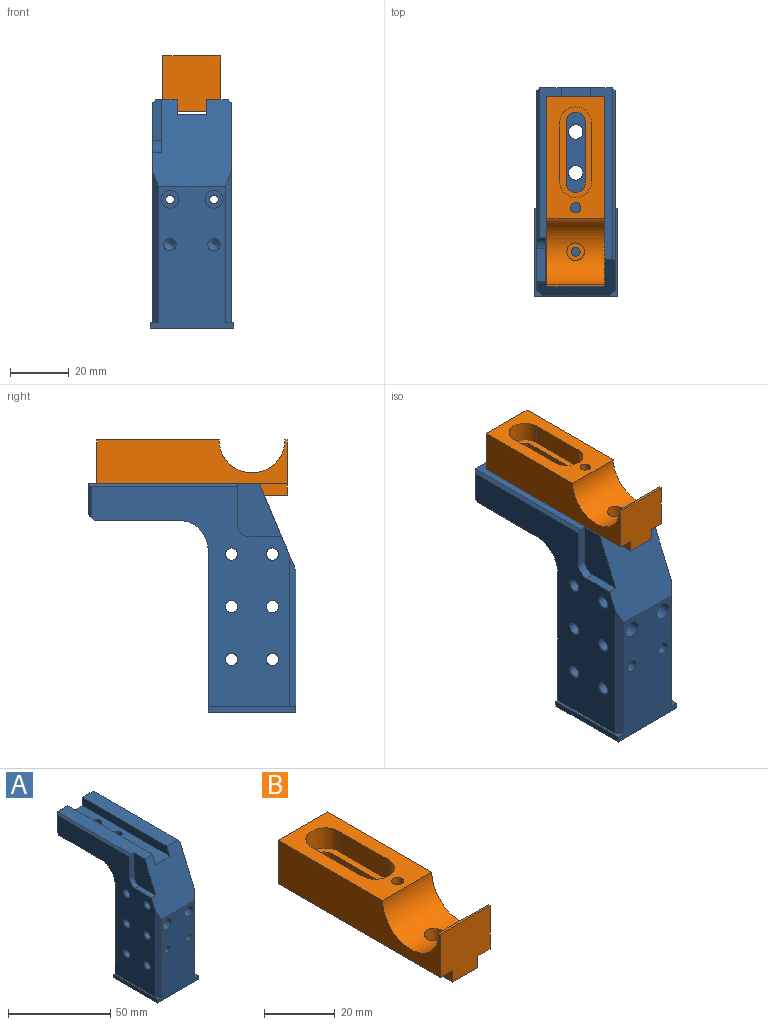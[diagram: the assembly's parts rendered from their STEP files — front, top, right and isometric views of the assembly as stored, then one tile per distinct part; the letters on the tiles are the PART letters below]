
ASSEMBLY  parts=2 mates=3
PART A: 53 faces, bbox 28.5x71x78 mm
  f0: cylinder r=10mm len=26.8mm, axis (-1,0,0), area 420mm2, adj f6,f7,f12,f14,f29
  f1: plane 58.48x7.3mm, normal (0,0,1), area 411.9mm2, adj f2,f3,f15,f17,f20,f48
  f2: plane 24.8x10.5mm, normal (0,1,0), area 210.4mm2, adj f1,f4,f19,f20,f21,f46,f51,f52
  f3: plane 29.5x26.8mm, normal (0,-0.92,0.39), area 735.1mm2, adj f1,f4,f8,f12,f14,f16,f17,f19
  f4: plane 58.48x7.5mm, normal (0,0,1), area 438.6mm2, adj f2,f3,f19,f47
  f5: plane 30x2mm, normal (-1,0,0), area 60mm2, adj f7,f8,f9,f13
  f6: plane 29x26.8mm, normal (0,0,-1), area 739mm2, adj f0,f12,f14,f28,f29,f46
  f7: plane 55.5x28.5mm, normal (0,1,0), area 1476.7mm2, adj f0,f5,f9,f10,f11,f12,f13,f14
  f8: plane 48.5x28.5mm, normal (0,-1,0), area 1032.9mm2, adj f3,f5,f9,f10,f11,f13,f30,f32
  f9: plane 30x28.5mm, normal (0,0,-1), area 799mm2, adj f5,f7,f8,f10,f41,f43,f44
  f10: plane 30x2mm, normal (1,0,0), area 60mm2, adj f7,f8,f9,f11
  f11: plane 30x2.85mm, normal (0,0,1), area 27.5mm2, adj f7,f8,f10,f12,f49
  f12: plane 75x68mm, normal (1,0,0), area 2377.7mm2, adj f0,f3,f6,f7,f11,f22,f23,f24
  f13: plane 30x2.85mm, normal (0,0,1), area 27.5mm2, adj f5,f7,f8,f14,f50
  f14: plane 75x68mm, normal (-1,0,0), area 2185.5mm2, adj f0,f3,f6,f7,f13,f15,f16,f18
  f15: plane 14x3mm, normal (0,-1,0), area 41.5mm2, adj f1,f14,f17,f18,f48
  f16: plane 11.12x3mm, normal (0,0,1), area 33.4mm2, adj f3,f14,f17,f18
  f17: plane 18x15.12mm, normal (-1,0,0), area 199.9mm2, adj f1,f3,f15,f16,f18
  f18: cylinder r=4mm len=4mm, axis (1,0,0), area 18.8mm2, adj f14,f15,f16,f17
  f19: plane 60.6x5mm, normal (-1,0,0), area 297.7mm2, adj f2,f3,f4,f21
  f20: plane 60.6x5mm, normal (1,0,0), area 297.7mm2, adj f1,f2,f3,f21
  f21: plane 60.6x10mm, normal (0,0,1), area 566.7mm2, adj f2,f3,f19,f20,f28,f29
  f22: cylinder r=2.1mm len=26.8mm, axis (1,0,0), area 353.6mm2, adj f12,f14
  f23: cylinder r=2.1mm len=26.8mm, axis (1,0,0), area 353.6mm2, adj f12,f14
  f24: cylinder r=2.1mm len=26.8mm, axis (1,0,0), area 353.6mm2, adj f12,f14
  f25: cylinder r=2.1mm len=26.8mm, axis (1,0,0), area 353.6mm2, adj f12,f14
  f26: cylinder r=2.1mm len=26.8mm, axis (1,0,0), area 353.6mm2, adj f12,f14
  f27: cylinder r=2.1mm len=26.8mm, axis (1,0,0), area 353.6mm2, adj f12,f14
  f28: cylinder r=2.5mm len=7.5mm, axis (0,0,1), area 117.8mm2, adj f6,f21
  f29: cylinder r=2.5mm len=7.5mm, axis (0,0,1), area 117.8mm2, adj f0,f6,f21
  f30: cylinder r=3mm len=6mm, axis (0,-1,0), area 84.8mm2, adj f8,f31
  f31: plane 6x6mm, normal (0,-1,0), area 21.2mm2, adj f30,f35
  f32: cylinder r=3mm len=6mm, axis (0,-1,0), area 84.8mm2, adj f8,f33
  f33: plane 6x6mm, normal (0,-1,0), area 21.2mm2, adj f32,f34
  f34: cylinder r=1.5mm len=25.5mm, axis (0,-1,0), area 240.3mm2, adj f7,f33
  f35: cylinder r=1.5mm len=25.5mm, axis (0,-1,0), area 240.3mm2, adj f7,f31
  f36: cone r=0mm half-angle=59deg, axis (0,-1,0), area 16.2mm2, adj f37
  f37: cylinder r=2.1mm len=15mm, axis (0,-1,0), area 197.9mm2, adj f8,f36
  f38: cone r=0mm half-angle=59deg, axis (0,-1,0), area 16.2mm2, adj f39
  f39: cylinder r=2.1mm len=15mm, axis (0,-1,0), area 197.9mm2, adj f8,f38
  f40: cone r=0mm half-angle=59deg, axis (0,0,-1), area 16.2mm2, adj f41
  f41: cylinder r=2.1mm len=12mm, axis (0,0,-1), area 158.3mm2, adj f9,f40
  f42: cone r=0mm half-angle=59deg, axis (0,0,-1), area 16.2mm2, adj f43
  f43: cylinder r=2.1mm len=12mm, axis (0,0,-1), area 158.3mm2, adj f9,f42
  f44: cylinder r=3mm len=15mm, axis (0,0,-1), area 282.7mm2, adj f9,f45
  f45: plane 6x6mm, normal (0,0,-1), area 28.3mm2, adj f44
  f46: plane 26.8x2mm, normal (0,0.71,-0.71), area 74.4mm2, adj f2,f6,f12,f14,f51,f52
  f47: plane 58.9x1mm, normal (0.71,0,0.71), area 82.3mm2, adj f3,f4,f12,f51
  f48: plane 51x1mm, normal (-0.71,0,0.71), area 71.4mm2, adj f1,f14,f15,f52
  f49: plane 51.21x2mm, normal (0.71,-0.71,0), area 138.2mm2, adj f3,f8,f11,f12
  f50: plane 51.21x2mm, normal (-0.71,-0.71,0), area 138.2mm2, adj f3,f8,f13,f14
  f51: plane 11.5x1mm, normal (0.71,0.71,0), area 14.8mm2, adj f2,f12,f46,f47
  f52: plane 11.5x1mm, normal (-0.71,0.71,0), area 14.8mm2, adj f2,f14,f46,f48
PART B: 25 faces, bbox 19.7x65x19 mm
  f0: cylinder r=11.25mm len=22.5mm, axis (1,0,0), area 667.7mm2, adj f3,f5,f9,f10,f21
  f1: plane 31x11mm, normal (0,0,1), area 145.4mm2, adj f13,f14,f15,f16,f17,f18,f19,f20
  f2: plane 65x10mm, normal (0,0,-1), area 463.6mm2, adj f6,f8,f11,f12,f17,f18,f19,f20
  f3: plane 41.75x19.7mm, normal (0,0,1), area 497.8mm2, adj f0,f8,f9,f10,f13,f14,f15,f16
  f4: plane 65x4.85mm, normal (0,0,-1), area 315.3mm2, adj f6,f8,f10,f11
  f5: plane 19.7x0.75mm, normal (0,0,1), area 14.8mm2, adj f0,f6,f9,f10
  f6: plane 19.7x19mm, normal (0,-1,0), area 335.5mm2, adj f2,f4,f5,f7,f9,f10,f11,f12
  f7: plane 65x4.85mm, normal (0,0,-1), area 315.2mm2, adj f6,f8,f9,f12
  f8: plane 19.7x19mm, normal (0,1,0), area 335.5mm2, adj f2,f3,f4,f7,f9,f10,f11,f12
  f9: plane 65x15mm, normal (-1,0,0), area 776.2mm2, adj f0,f3,f5,f6,f7,f8
  f10: plane 65x15mm, normal (1,0,0), area 776.2mm2, adj f0,f3,f4,f5,f6,f8
  f11: plane 65x4mm, normal (1,0,0), area 260mm2, adj f2,f4,f6,f8
  f12: plane 65x4mm, normal (-1,0,0), area 260mm2, adj f2,f6,f7,f8
  f13: plane 20x7mm, normal (1,0,0), area 140mm2, adj f1,f3,f14,f16
  f14: cylinder r=5.5mm len=11mm, axis (0,0,1), area 121mm2, adj f1,f3,f13,f15
  f15: plane 20x7mm, normal (-1,0,0), area 140mm2, adj f1,f3,f14,f16
  f16: cylinder r=5.5mm len=11mm, axis (0,0,1), area 121mm2, adj f1,f3,f13,f15
  f17: plane 21x12mm, normal (1,0,0), area 252mm2, adj f1,f2,f18,f20
  f18: cylinder r=3.25mm len=12mm, axis (0,0,1), area 122.5mm2, adj f1,f2,f17,f19
  f19: plane 21x12mm, normal (-1,0,0), area 252mm2, adj f1,f2,f18,f20
  f20: cylinder r=3.25mm len=12mm, axis (0,0,1), area 122.5mm2, adj f1,f2,f17,f19
  f21: cylinder r=3mm len=6mm, axis (0,0,1), area 88.6mm2, adj f0,f22
  f22: plane 6x6mm, normal (0,0,1), area 21.2mm2, adj f21,f23
  f23: cylinder r=1.5mm len=3.25mm, axis (0,0,1), area 30.6mm2, adj f2,f22
  f24: cylinder r=1.75mm len=19mm, axis (0,0,1), area 208.9mm2, adj f2,f3
PLACE A t=(-1.49,6.83,-10.1)mm
PLACE B t=(-5.99,24.73,42.83)mm
MATE parallel B.f8 <-> A.f2  axis (0,1,0) through (-15.84,58.98,41.53)mm
MATE planar B.f4 <-> A.f4  axis (0,0,-1) through (-8.42,26.48,35.16)mm
MATE planar B.f12 <-> A.f20  axis (-1,0,0) through (-20.84,26.48,33.16)mm
